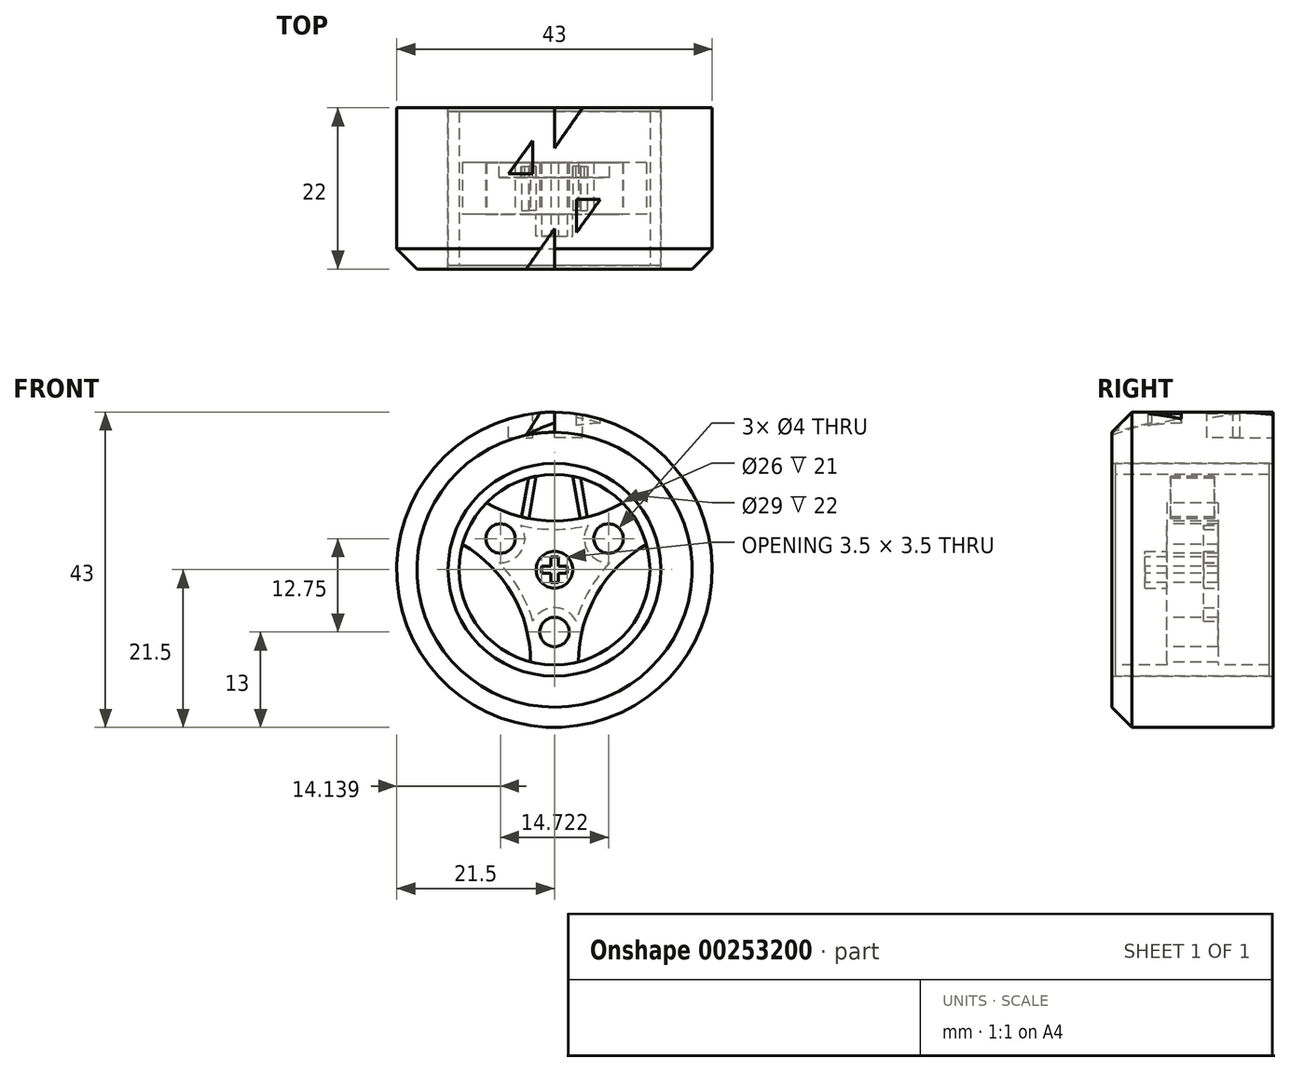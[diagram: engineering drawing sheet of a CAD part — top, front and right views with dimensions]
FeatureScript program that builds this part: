
annotation { "Feature Type Name" : "Feature", "Feature Type Description" : "" }
export const myFeature = defineFeature(function(context is Context, id is Id, definition is map)
    precondition{}
    {
        {
            var Q0;
            Q0=qCreatedBy(makeId("Front.planeOp"),FACE);
            var sketch = newSketch(context, id + "F0", { "sketchPlane" : qUnion([Q0])});
            skCircle(sketch, "E0", {"center": v(0, 0) * mm, "radius": 21.5 * mm});
            skCircle(sketch, "E1", {"center": v(0, 0) * mm, "radius": 14.5 * mm});
            skSolve(sketch);
        }
        {
            var Q0;
            Q0 = qSketchRegion(id + "F0", true);
            extrude(context, id + "F1", {"entities" : qUnion([Q0]), "depth" : 11 * mm, "hasSecondDirection" : true, "secondDirectionOppositeDirection" : true, "secondDirectionDepth" : 11 * mm});
        }
        {
            var Q0;
            Q0=qCreatedBy(makeId("Top.planeOp"),FACE);
            cPlane(context, id + "F2", {"entities" : qUnion([Q0]), "cplaneType" : CPlaneType.OFFSET, "offset" : 21.5 * mm, "width" : 150 * mm, "height" : 150 * mm});
        }
        {
            var Q0;
            Q0=qCreatedBy(id+"F2.planeOp",FACE);
            var sketch = newSketch(context, id + "F3", { "sketchPlane" : qUnion([Q0])});
            skLineSegment(sketch, "E2", {"start": v(0, -11) * mm, "end": v(0, -5.5) * mm});
            skLineSegment(sketch, "E3", {"start": v(0, -5.5) * mm, "end": v(-3.85, -11) * mm});
            skLineSegment(sketch, "E4", {"start": v(-3.85, -11) * mm, "end": v(0, -11) * mm});
            skLineSegment(sketch, "E5", {"start": v(0, 0) * mm, "end": v(0, -5.5) * mm, "construction": true});
            skLineSegment(sketch, "E6", {"start": v(3, -1.5) * mm, "end": v(3, -6) * mm});
            skLineSegment(sketch, "E7", {"start": v(3, -6) * mm, "end": v(6.25, -1.5) * mm});
            skLineSegment(sketch, "E8", {"start": v(6.25, -1.5) * mm, "end": v(3, -1.5) * mm});
            skLineSegment(sketch, "E9", {"start": v(3, -6) * mm, "end": v(0, -6) * mm, "construction": true});
            skLineSegment(sketch, "E10", {"start": v(0, 11) * mm, "end": v(0, 5.5) * mm});
            skLineSegment(sketch, "E11", {"start": v(0, 5.5) * mm, "end": v(3.85, 11) * mm});
            skLineSegment(sketch, "E12", {"start": v(3.85, 11) * mm, "end": v(0, 11) * mm});
            skLineSegment(sketch, "E13", {"start": v(-3, 6.5) * mm, "end": v(-3, 2) * mm});
            skLineSegment(sketch, "E14", {"start": v(-3, 2) * mm, "end": v(-6.25, 2) * mm});
            skLineSegment(sketch, "E15", {"start": v(-6.25, 2) * mm, "end": v(-3, 6.5) * mm});
            skSolve(sketch);
        }
        {
            var Q0;
            Q0=makeQuery(id+"F1.opExtrude","CAP_FACE",FACE,{"disambiguationData":[OSD([sQuery(id+"F0.wireOp",EDGE,"E0"),sQuery(id+"F0.wireOp",EDGE,"E1")])],"isStart":false});
            var sketch = newSketch(context, id + "F4", { "sketchPlane" : qUnion([Q0])});
            skLineSegment(sketch, "E16", {"start": v(-2, 18) * mm, "end": v(2, 18) * mm});
            skLineSegment(sketch, "E17", {"start": v(0, 18) * mm, "end": v(0, 0) * mm, "construction": true});
            skLineSegment(sketch, "E18", {"start": v(0, 21.5) * mm, "end": v(0, 14.5) * mm, "construction": true});
            skPoint(sketch, "E19", {"position": v(0, 18) * mm});
            skSolve(sketch);
        }
        {
            var Q0;
            Q0=sQuery(id+"F4.wireOp",VERTEX,"E16.end");
            var Q1;
            Q1=sQuery(id+"F4.wireOp",VERTEX,"E16.start");
            var Q2;
            Q2=sQuery(id+"F3.wireOp",VERTEX,"E5.start");
            cPlane(context, id + "F5", {"entities" : qUnion([Q0, Q1, Q2]), "cplaneType" : CPlaneType.THREE_POINT, "offset" : 25 * mm, "width" : 150 * mm, "height" : 150 * mm});
        }
        {
            var Q0;
            Q0 = qSketchRegion(id + "F3", true);
            var Q1;
            Q1=qCreatedBy(id+"F5.planeOp",FACE);
            extrude(context, id + "F6", {"entities" : qUnion([Q0]), "operationType" : NewBodyOperationType.REMOVE, "oppositeDirection" : true, "endBoundEntityFace" : qUnion([Q1]), "depth" : 3.5 * mm});
        }
        {
            var Q0;
            Q0=qCreatedBy(makeId("Top.planeOp"),FACE);
            var sketch = newSketch(context, id + "F7", { "sketchPlane" : qUnion([Q0])});
            skLineSegment(sketch, "E20", {"start": v(0, -33.63) * mm, "end": v(0, 33.63) * mm, "construction": true});
            skSolve(sketch);
        }
        {
            var Q0;
            Q0=qCreatedBy(makeId("Right.planeOp"),FACE);
            var sketch = newSketch(context, id + "F8", { "sketchPlane" : qUnion([Q0])});
            skLineSegment(sketch, "E21", {"start": v(-11, 18.75) * mm, "end": v(-11, 21.5) * mm});
            skLineSegment(sketch, "E22", {"start": v(-11, 21.5) * mm, "end": v(-8.25, 21.5) * mm});
            skLineSegment(sketch, "E23", {"start": v(-8.25, 21.5) * mm, "end": v(-11, 18.75) * mm});
            skSolve(sketch);
        }
        {
            var Q0;
            Q0 = qSketchRegion(id + "F8", true);
            var Q1;
            Q1=makeQuery(id+"F1.opExtrude","CAP_EDGE",EDGE,{"disambiguationData":[OSD([sQuery(id+"F0.wireOp",EDGE,"E1")])],"isStart":false});
            revolve(context, id + "F9", {"operationType" : NewBodyOperationType.REMOVE, "entities" : qUnion([Q0]), "axis" : qUnion([Q1]), "revolveType" : RevolveType.FULL, "oppositeDirection" : true});
        }
        {
            var Q0;
            Q0=qCreatedBy(makeId("Right.planeOp"),FACE);
            var sketch = newSketch(context, id + "F10", { "sketchPlane" : qUnion([Q0])});
            skLineSegment(sketch, "E24", {"start": v(-11, 18.75) * mm, "end": v(-11, 18) * mm});
            skLineSegment(sketch, "E25", {"start": v(-11, 18) * mm, "end": v(0, 18) * mm});
            skLineSegment(sketch, "E26", {"start": v(0, 18) * mm, "end": v(0, 21.29) * mm});
            skLineSegment(sketch, "E27", {"start": v(0, 21.29) * mm, "end": v(-11, 18.75) * mm});
            skSolve(sketch);
        }
        {
            var Q0;
            Q0 = qSketchRegion(id + "F10", true);
            var Q1;
            Q1=makeQuery(id+"F1.opExtrude","CAP_EDGE",EDGE,{"disambiguationData":[OSD([sQuery(id+"F0.wireOp",EDGE,"E1")])],"isStart":false});
            revolve(context, id + "F11", {"operationType" : NewBodyOperationType.ADD, "entities" : qUnion([Q0]), "axis" : qUnion([Q1]), "revolveType" : RevolveType.FULL});
        }
        {
            var Q0;
            Q0=qCreatedBy(makeId("Right.planeOp"),FACE);
            var sketch = newSketch(context, id + "F12", { "sketchPlane" : qUnion([Q0])});
            skLineSegment(sketch, "E28", {"start": v(-10.5, 14.5) * mm, "end": v(-10.5, 13) * mm});
            skLineSegment(sketch, "E29", {"start": v(-10.5, 13) * mm, "end": v(-3.5, 13) * mm});
            skLineSegment(sketch, "E30", {"start": v(-3.5, 13) * mm, "end": v(-3.5, 0) * mm});
            skLineSegment(sketch, "E31", {"start": v(-3.5, 0) * mm, "end": v(3.5, 0) * mm});
            skLineSegment(sketch, "E32", {"start": v(3.5, 0) * mm, "end": v(3.5, 13) * mm});
            skLineSegment(sketch, "E33", {"start": v(3.5, 13) * mm, "end": v(10.5, 13) * mm});
            skLineSegment(sketch, "E34", {"start": v(10.5, 13) * mm, "end": v(10.5, 14.5) * mm});
            skLineSegment(sketch, "E35", {"start": v(10.5, 14.5) * mm, "end": v(-10.5, 14.5) * mm});
            skPoint(sketch, "E36", {"position": v(0, 0) * mm});
            skSolve(sketch);
        }
        {
            var Q0;
            Q0 = qSketchRegion(id + "F12", true);
            var Q1;
            Q1=sQuery(id+"F7.wireOp",EDGE,"E20");
            revolve(context, id + "F13", {"entities" : qUnion([Q0]), "axis" : qUnion([Q1]), "revolveType" : RevolveType.FULL});
        }
        {
            var Q0;
            Q0=makeQuery(id+"F13.opRevolve","SWEPT_FACE",FACE,{"disambiguationData":[OSD([sQuery(id+"F12.wireOp",EDGE,"E30")])]});
            var sketch = newSketch(context, id + "F14", { "sketchPlane" : qUnion([Q0])});
            skArc(sketch, "E37", {"start": v(-9.26, 9.13) * mm, "mid": v(0, 6.65) * mm, "end": v(9.26, 9.13) * mm});
            skArc(sketch, "E38", {"start": v(-3.28, -12.58) * mm, "mid": v(-5.76, -3.32) * mm, "end": v(-12.53, 3.45) * mm});
            skArc(sketch, "E39", {"start": v(12.53, 3.45) * mm, "mid": v(5.76, -3.32) * mm, "end": v(3.28, -12.58) * mm});
            skPoint(sketch, "E40", {"position": v(0, -11.26) * mm});
            skArc(sketch, "E41.0", {"start": v(-12.53, 3.45) * mm, "mid": v(-11.26, -6.5) * mm, "end": v(-3.28, -12.58) * mm});
            skArc(sketch, "E42.trimOffspring", {"start": v(9.26, 9.13) * mm, "mid": v(0, 13) * mm, "end": v(-9.26, 9.13) * mm});
            skArc(sketch, "E43.trimOffspring", {"start": v(3.28, -12.58) * mm, "mid": v(11.26, -6.5) * mm, "end": v(12.53, 3.45) * mm});
            skLineSegment(sketch, "E44", {"start": v(-9.26, 9.13) * mm, "end": v(9.26, 9.13) * mm, "construction": true});
            skLineSegment(sketch, "E45", {"start": v(12.53, 3.45) * mm, "end": v(3.28, -12.58) * mm, "construction": true});
            skLineSegment(sketch, "E46", {"start": v(-3.28, -12.58) * mm, "end": v(-12.53, 3.45) * mm, "construction": true});
            skLineSegment(sketch, "E47", {"start": v(-9.26, 9.13) * mm, "end": v(-1.97, 4.92) * mm, "construction": true});
            skCircle(sketch, "E48", {"center": v(7.36, 4.25) * mm, "radius": 2 * mm});
            skCircle(sketch, "E49", {"center": v(-7.36, 4.25) * mm, "radius": 2 * mm});
            skCircle(sketch, "E50", {"center": v(0, -8.5) * mm, "radius": 2 * mm});
            skLineSegment(sketch, "E51", {"start": v(0, -8.5) * mm, "end": v(0, 0) * mm, "construction": true});
            skLineSegment(sketch, "E52", {"start": v(7.36, 4.25) * mm, "end": v(0, 0) * mm, "construction": true});
            skLineSegment(sketch, "E53", {"start": v(0, 0) * mm, "end": v(-7.36, 4.25) * mm, "construction": true});
            skLineSegment(sketch, "E54", {"start": v(-7.9, -4.56) * mm, "end": v(0, 0) * mm, "construction": true});
            skLineSegment(sketch, "E55", {"start": v(0, 0) * mm, "end": v(0, 9.13) * mm, "construction": true});
            skLineSegment(sketch, "E56", {"start": v(0, 9.13) * mm, "end": v(0, 0) * mm});
            skLineSegment(sketch, "E57", {"start": v(7.9, -4.56) * mm, "end": v(0, 0) * mm, "construction": true});
            skLineSegment(sketch, "E58", {"start": v(-12.53, 3.45) * mm, "end": v(-9.26, 9.13) * mm, "construction": true});
            skSolve(sketch);
        }
        {
            var Q0;
            Q0 = qSketchRegion(id + "F14", true);
            extrude(context, id + "F15", {"entities" : qUnion([Q0]), "operationType" : NewBodyOperationType.REMOVE, "oppositeDirection" : true, "depth" : 25 * mm});
        }
        {
            var Q0;
            Q0=makeQuery(id+"F13.opRevolve","SWEPT_FACE",FACE,{"disambiguationData":[OSD([sQuery(id+"F12.wireOp",EDGE,"E30")])]});
            var sketch = newSketch(context, id + "F16", { "sketchPlane" : qUnion([Q0])});
            skCircle(sketch, "E59", {"center": v(0, 0) * mm, "radius": 2.5 * mm});
            skSolve(sketch);
        }
        {
            var Q0;
            Q0 = qSketchRegion(id + "F16", true);
            extrude(context, id + "F17", {"entities" : qUnion([Q0]), "operationType" : NewBodyOperationType.ADD, "depth" : 3 * mm});
        }
        {
            var Q0;
            Q0=makeQuery(id+"F17.opExtrude","CAP_FACE",FACE,{"disambiguationData":[OSD([sQuery(id+"F16.wireOp",EDGE,"E59")])],"isStart":false});
            var sketch = newSketch(context, id + "F18", { "sketchPlane" : qUnion([Q0])});
            skLineSegment(sketch, "E60", {"start": v(-0.5, 0.5) * mm, "end": v(-0.5, 1.75) * mm});
            skLineSegment(sketch, "E61", {"start": v(-0.5, 1.75) * mm, "end": v(0.5, 1.75) * mm});
            skLineSegment(sketch, "E62", {"start": v(0.5, 1.75) * mm, "end": v(0.5, 0.5) * mm});
            skLineSegment(sketch, "E63", {"start": v(0.5, 0.5) * mm, "end": v(1.75, 0.5) * mm});
            skLineSegment(sketch, "E64", {"start": v(1.75, 0.5) * mm, "end": v(1.75, -0.5) * mm});
            skLineSegment(sketch, "E65", {"start": v(1.75, -0.5) * mm, "end": v(0.5, -0.5) * mm});
            skLineSegment(sketch, "E66", {"start": v(0.5, -0.5) * mm, "end": v(0.5, -1.75) * mm});
            skLineSegment(sketch, "E67", {"start": v(0.5, -1.75) * mm, "end": v(-0.5, -1.75) * mm});
            skLineSegment(sketch, "E68", {"start": v(-0.5, -1.75) * mm, "end": v(-0.5, -0.5) * mm});
            skLineSegment(sketch, "E69", {"start": v(-0.5, -0.5) * mm, "end": v(-1.75, -0.5) * mm});
            skLineSegment(sketch, "E70", {"start": v(-1.75, -0.5) * mm, "end": v(-1.75, 0.5) * mm});
            skLineSegment(sketch, "E71", {"start": v(-1.75, 0.5) * mm, "end": v(-0.5, 0.5) * mm});
            skLineSegment(sketch, "E72", {"start": v(-0.5, 0.5) * mm, "end": v(0.5, -0.5) * mm, "construction": true});
            skLineSegment(sketch, "E73", {"start": v(-0.5, -0.5) * mm, "end": v(0.5, 0.5) * mm, "construction": true});
            skSolve(sketch);
        }
        {
            var Q0;
            Q0 = qSketchRegion(id + "F18", true);
            extrude(context, id + "F19", {"entities" : qUnion([Q0]), "operationType" : NewBodyOperationType.REMOVE, "endBound" : BoundingType.THROUGH_ALL, "oppositeDirection" : true, "depth" : 25 * mm});
        }
        {
            var Q0;
            Q0=makeQuery(id+"F13.opRevolve","SWEPT_FACE",FACE,{"disambiguationData":[OSD([sQuery(id+"F12.wireOp",EDGE,"E32")])]});
            var sketch = newSketch(context, id + "F20", { "sketchPlane" : qUnion([Q0])});
            skArc(sketch, "E74", {"start": v(-7.53, 0.95) * mm, "mid": v(-4.5, 2.6) * mm, "end": v(-4.6, 6.05) * mm});
            skArc(sketch, "E75", {"start": v(4.6, 6.05) * mm, "mid": v(4.5, 2.6) * mm, "end": v(7.53, 0.95) * mm});
            skArc(sketch, "E76", {"start": v(-4.6, 6.05) * mm, "mid": v(0, 5.5) * mm, "end": v(4.6, 6.05) * mm});
            skArc(sketch, "E77", {"start": v(-2.94, -7) * mm, "mid": v(-4.77, -2.75) * mm, "end": v(-7.53, 0.95) * mm});
            skArc(sketch, "E78", {"start": v(2.94, -7) * mm, "mid": v(0, -5.2) * mm, "end": v(-2.94, -7) * mm});
            skArc(sketch, "E79", {"start": v(7.53, 0.95) * mm, "mid": v(4.77, -2.75) * mm, "end": v(2.94, -7) * mm});
            skLineSegment(sketch, "E80", {"start": v(-2.94, -7) * mm, "end": v(2.94, -7) * mm, "construction": true});
            skLineSegment(sketch, "E81", {"start": v(-7.53, 0.95) * mm, "end": v(-4.6, 6.05) * mm, "construction": true});
            skLineSegment(sketch, "E82", {"start": v(4.6, 6.05) * mm, "end": v(7.53, 0.95) * mm, "construction": true});
            skLineSegment(sketch, "E83", {"start": v(-6.06, 3.5) * mm, "end": v(0, 0) * mm, "construction": true});
            skLineSegment(sketch, "E84", {"start": v(6.06, 3.5) * mm, "end": v(0, 0) * mm, "construction": true});
            skLineSegment(sketch, "E85", {"start": v(0, -7) * mm, "end": v(0, 0) * mm, "construction": true});
            skPoint(sketch, "E85.endSnap0", {"position": v(0, -5.2) * mm});
            skCircle(sketch, "E86.0", {"center": v(0, 0) * mm, "radius": 2.5 * mm});
            skSolve(sketch);
        }
        {
            var Q0;
            Q0 = qSketchRegion(id + "F20", true);
            extrude(context, id + "F21", {"entities" : qUnion([Q0]), "operationType" : NewBodyOperationType.REMOVE, "oppositeDirection" : true, "depth" : 2 * mm});
        }
        {
            var Q0;
            Q0=qCreatedBy(makeId("Front.planeOp"),FACE);
            cPlane(context, id + "F22", {"entities" : qUnion([Q0]), "cplaneType" : CPlaneType.OFFSET, "offset" : 3 * mm, "width" : 150 * mm, "height" : 150 * mm});
        }
        {
            var Q0;
            Q0=qCreatedBy(id+"F22.planeOp",FACE);
            var sketch = newSketch(context, id + "F23", { "sketchPlane" : qUnion([Q0])});
            skArc(sketch, "E87.0", {"start": v(-4.48, 7.2) * mm, "mid": v(-4, 7.08) * mm, "end": v(-3.5, 6.98) * mm});
            skLineSegment(sketch, "E88", {"start": v(-4.48, 7.2) * mm, "end": v(-3.56, 12.5) * mm});
            skLineSegment(sketch, "E89", {"start": v(-2.5, 12.76) * mm, "end": v(-3.5, 6.98) * mm});
            skLineSegment(sketch, "E90", {"start": v(3.5, 6.98) * mm, "end": v(2.5, 12.76) * mm});
            skLineSegment(sketch, "E91", {"start": v(3.56, 12.5) * mm, "end": v(4.48, 7.2) * mm});
            skArc(sketch, "E92.trimOffspring", {"start": v(-2.5, 12.76) * mm, "mid": v(-3.03, 12.64) * mm, "end": v(-3.56, 12.5) * mm});
            skArc(sketch, "E93.trimOffspring", {"start": v(3.56, 12.5) * mm, "mid": v(3.03, 12.64) * mm, "end": v(2.5, 12.76) * mm});
            skPoint(sketch, "E94.orphan", {"position": v(9.26, 9.13) * mm});
            skArc(sketch, "E95.trimOffspring", {"start": v(3.5, 6.98) * mm, "mid": v(4, 7.08) * mm, "end": v(4.48, 7.2) * mm});
            skPoint(sketch, "E96.orphan", {"position": v(-9.26, 9.13) * mm});
            skLineSegment(sketch, "E97", {"start": v(-3.5, 6.98) * mm, "end": v(3.5, 6.98) * mm, "construction": true});
            skLineSegment(sketch, "E98", {"start": v(-2.5, 12.76) * mm, "end": v(2.5, 12.76) * mm, "construction": true});
            skLineSegment(sketch, "E99", {"start": v(3.99, 10.04) * mm, "end": v(3, 9.87) * mm, "construction": true});
            skLineSegment(sketch, "E100", {"start": v(-3, 9.87) * mm, "end": v(-3.99, 10.04) * mm, "construction": true});
            skLineSegment(sketch, "E101", {"start": v(0, 12.76) * mm, "end": v(0, 0) * mm, "construction": true});
            skPoint(sketch, "E102", {"position": v(0, 6.98) * mm});
            skLineSegment(sketch, "E103", {"start": v(-3.5, 9.95) * mm, "end": v(3.5, 9.95) * mm, "construction": true});
            skSolve(sketch);
        }
        {
            var Q0;
            Q0 = qSketchRegion(id + "F23", true);
            extrude(context, id + "F24", {"entities" : qUnion([Q0]), "operationType" : NewBodyOperationType.ADD, "oppositeDirection" : true, "depth" : 6 * mm});
        }
    });
